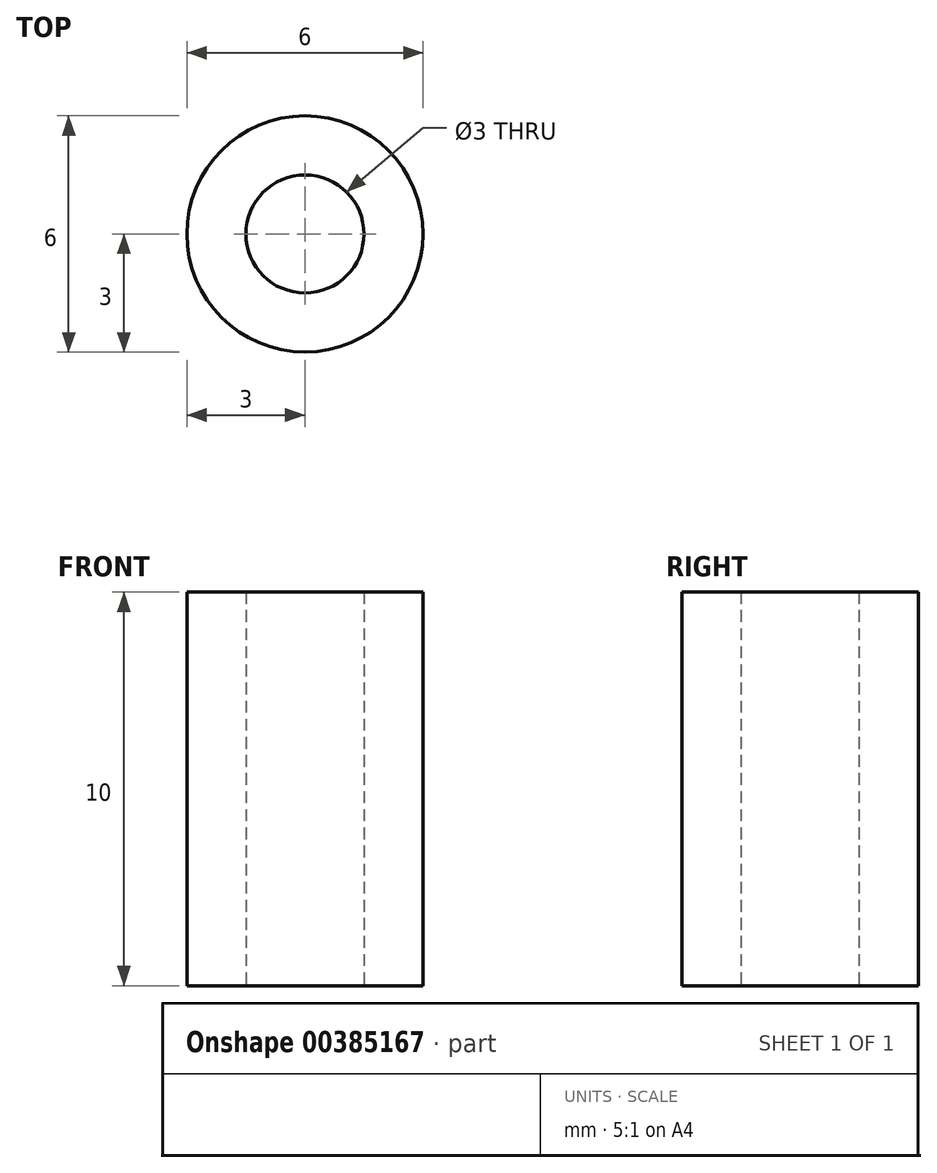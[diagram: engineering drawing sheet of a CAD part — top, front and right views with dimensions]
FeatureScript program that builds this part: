
annotation { "Feature Type Name" : "Feature", "Feature Type Description" : "" }
export const myFeature = defineFeature(function(context is Context, id is Id, definition is map)
    precondition{}
    {
        {
            var Q0;
            Q0=qCreatedBy(makeId("Top.planeOp"),FACE);
            var sketch = newSketch(context, id + "F0", { "sketchPlane" : qUnion([Q0])});
            skCircle(sketch, "E0", {"center": v(0, 0) * mm, "radius": 1.5 * mm});
            skCircle(sketch, "E1", {"center": v(0, 0) * mm, "radius": 3 * mm});
            skSolve(sketch);
        }
        {
            var Q0;
            Q0=makeQuery(id+"F0.imprint","IMPRINT",FACE,{"disambiguationData":[TD([[makeQuery(id+"F0.imprint","IMPRINT",EDGE,{"derivedFrom":sQuery(id+"F0.wireOp",EDGE,"E0")}),-1.0]])]});
            extrude(context, id + "F1", {"entities" : qUnion([Q0]), "depth" : 10 * mm, "offsetDistance" : 25 * mm});
        }
    });
